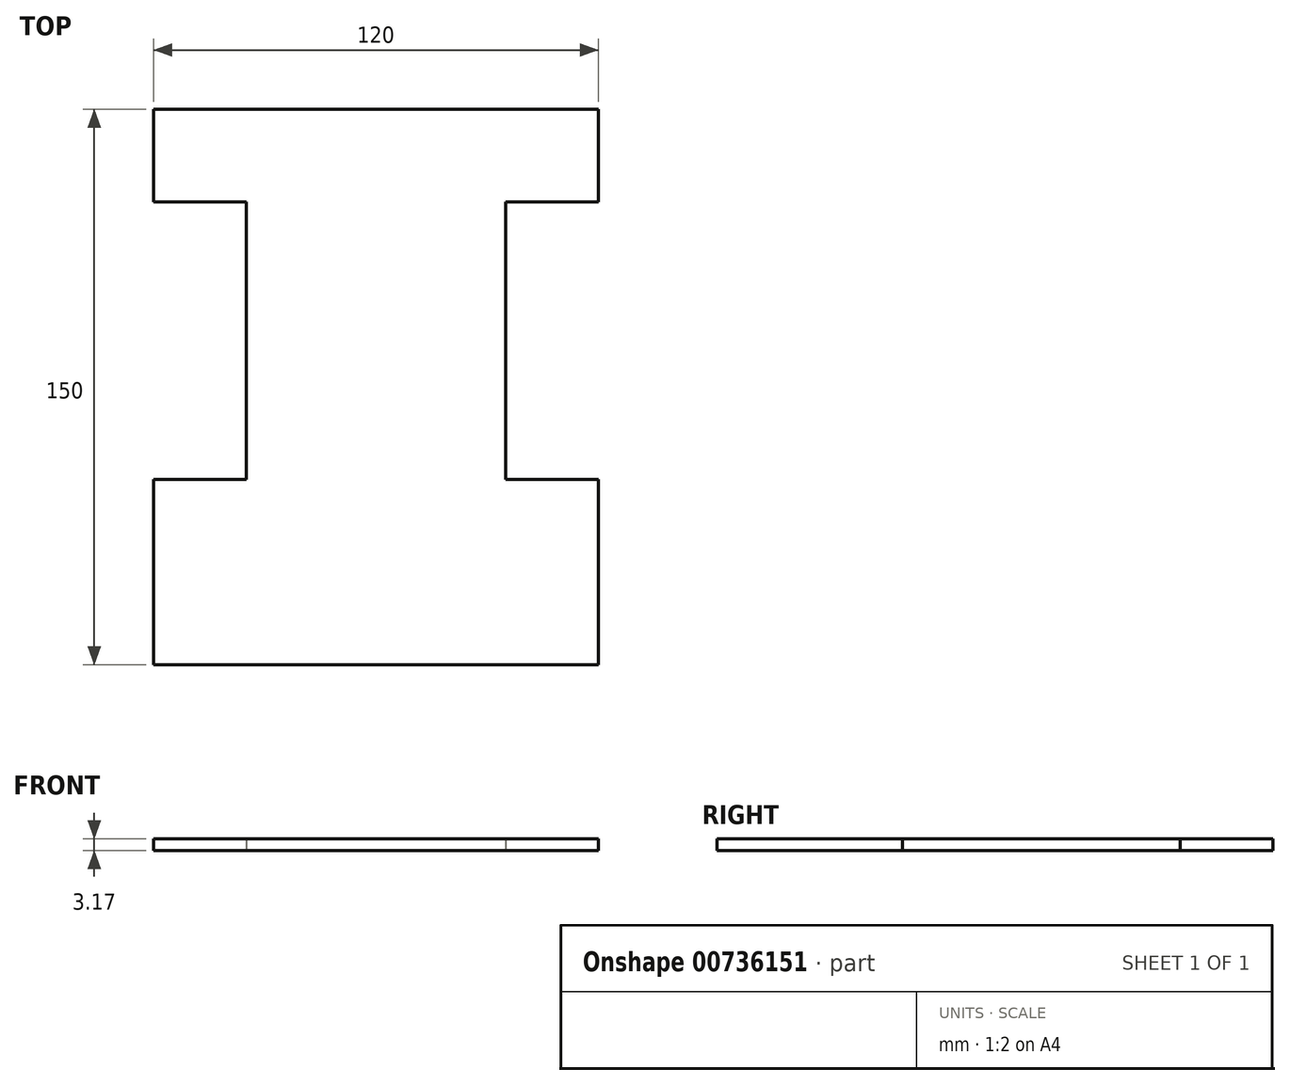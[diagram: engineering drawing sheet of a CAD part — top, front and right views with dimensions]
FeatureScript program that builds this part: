
annotation { "Feature Type Name" : "Feature", "Feature Type Description" : "" }
export const myFeature = defineFeature(function(context is Context, id is Id, definition is map)
    precondition{}
    {
        {
            var Q0;
            Q0=qCreatedBy(makeId("Top.planeOp"),FACE);
            var sketch = newSketch(context, id + "F0", { "sketchPlane" : qUnion([Q0])});
            skLineSegment(sketch, "E0.bottom", {"start": v(-249.32, 62.9) * mm, "end": v(-129.32, 62.9) * mm});
            skLineSegment(sketch, "E0.top", {"start": v(-249.32, -87.1) * mm, "end": v(-129.32, -87.1) * mm});
            skLineSegment(sketch, "E0.right", {"start": v(-129.32, 62.9) * mm, "end": v(-129.32, 37.9) * mm});
            skPoint(sketch, "E1", {"position": v(-249.32, -37.1) * mm});
            skLineSegment(sketch, "E2", {"start": v(-249.32, -37.1) * mm, "end": v(-249.32, -87.1) * mm});
            skPoint(sketch, "E3", {"position": v(-189.32, 62.9) * mm});
            skPoint(sketch, "E4", {"position": v(-189.32, -87.1) * mm});
            skLineSegment(sketch, "E5.trimOffspring", {"start": v(-129.32, -37.1) * mm, "end": v(-129.32, -87.1) * mm});
            skLineSegment(sketch, "E6", {"start": v(-249.32, 37.9) * mm, "end": v(-249.32, 62.9) * mm});
            skLineSegment(sketch, "E7.bottom", {"start": v(-249.32, 37.9) * mm, "end": v(-224.32, 37.9) * mm});
            skLineSegment(sketch, "E7.top", {"start": v(-249.32, -37.1) * mm, "end": v(-224.32, -37.1) * mm});
            skLineSegment(sketch, "E7.right", {"start": v(-224.32, 37.9) * mm, "end": v(-224.32, -37.1) * mm});
            skLineSegment(sketch, "E8.bottom", {"start": v(-129.32, 37.9) * mm, "end": v(-154.32, 37.9) * mm});
            skLineSegment(sketch, "E8.top", {"start": v(-129.32, -37.1) * mm, "end": v(-154.32, -37.1) * mm});
            skLineSegment(sketch, "E8.right", {"start": v(-154.32, 37.9) * mm, "end": v(-154.32, -37.1) * mm});
            skSolve(sketch);
        }
        {
            var Q0;
            Q0=makeQuery(id+"F0.imprint","IMPRINT",FACE,{"disambiguationData":[TD([[makeQuery(id+"F0.imprint","IMPRINT",EDGE,{"derivedFrom":sQuery(id+"F0.wireOp",EDGE,"E0.bottom")}),-1.0]])]});
            extrude(context, id + "F1", {"entities" : qUnion([Q0]), "depth" : 3.17 * mm, "offsetDistance" : 25 * mm});
        }
    });
